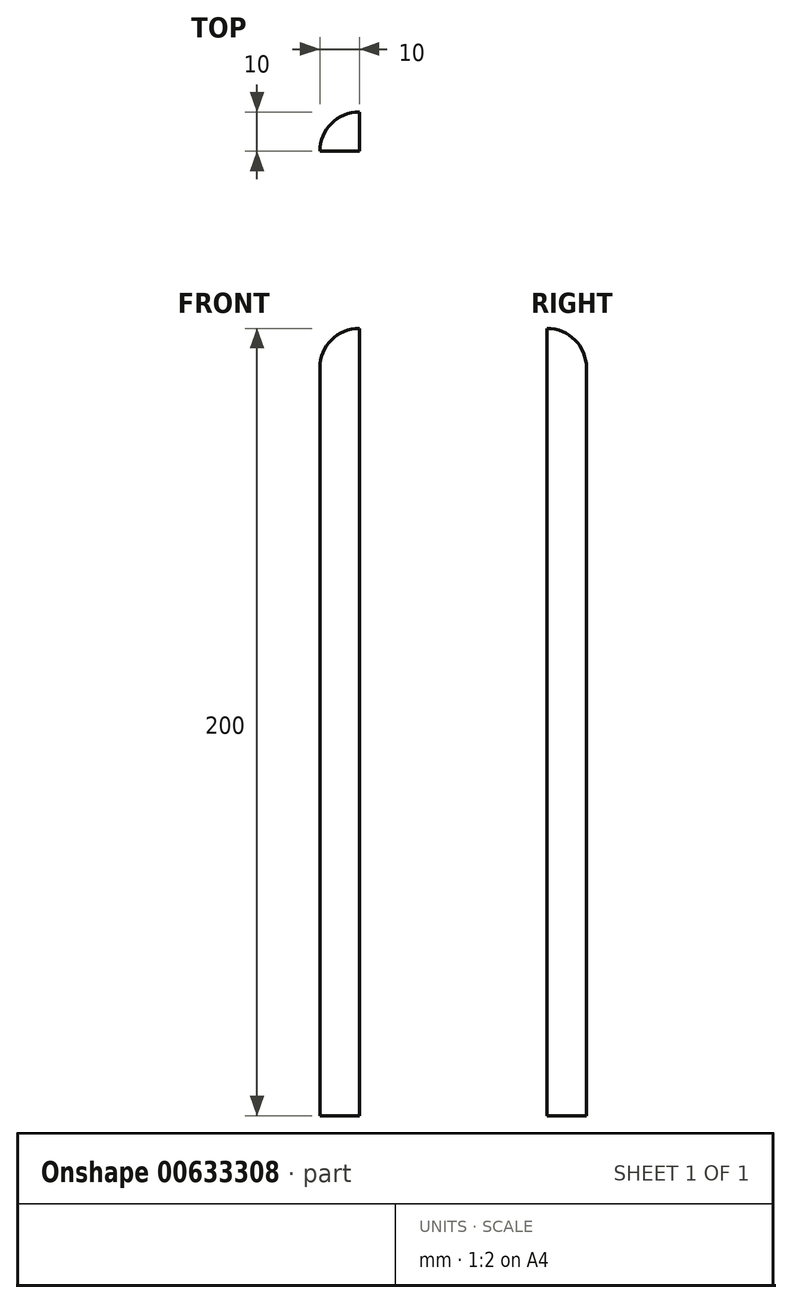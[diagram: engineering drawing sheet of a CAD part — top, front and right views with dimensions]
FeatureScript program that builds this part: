
annotation { "Feature Type Name" : "Feature", "Feature Type Description" : "" }
export const myFeature = defineFeature(function(context is Context, id is Id, definition is map)
    precondition{}
    {
        {
            var Q0;
            Q0=qCreatedBy(makeId("Top.planeOp"),FACE);
            var sketch = newSketch(context, id + "F0", { "sketchPlane" : qUnion([Q0])});
            skLineSegment(sketch, "E0.bottom", {"start": v(5, 5) * mm, "end": v(5, 5) * mm});
            skLineSegment(sketch, "E0.top", {"start": v(5, -5) * mm, "end": v(-5, -5) * mm});
            skLineSegment(sketch, "E0.left", {"start": v(5, 5) * mm, "end": v(5, -5) * mm});
            skLineSegment(sketch, "E0.right", {"start": v(-5, -5) * mm, "end": v(-5, -5) * mm});
            skPoint(sketch, "E0.middle", {"position": v(0, 0) * mm});
            skPoint(sketch, "E1.visualSharp", {"position": v(-5, 5) * mm});
            skArc(sketch, "E1.filletArc", {"start": v(5, 5) * mm, "mid": v(-2.07, 2.07) * mm, "end": v(-5, -5) * mm});
            skSolve(sketch);
        }
        {
            var Q0;
            Q0 = qSketchRegion(id + "F0", true);
            extrude(context, id + "F1", {"entities" : qUnion([Q0]), "endBound" : BoundingType.SYMMETRIC, "depth" : 200 * mm, "offsetDistance" : 25 * mm});
        }
        {
            var Q0;
            Q0=makeQuery(id+"F1.opExtrude","CAP_EDGE",EDGE,{"disambiguationData":[OSD([sQuery(id+"F0.wireOp",EDGE,"E1.filletArc")])],"isStart":false});
            fillet(context, id + "F2", {"entities" : qUnion([Q0]), "radius" : 10 * mm, "tangentPropagation" : true, "allowEdgeOverflow" : false});
        }
    });
